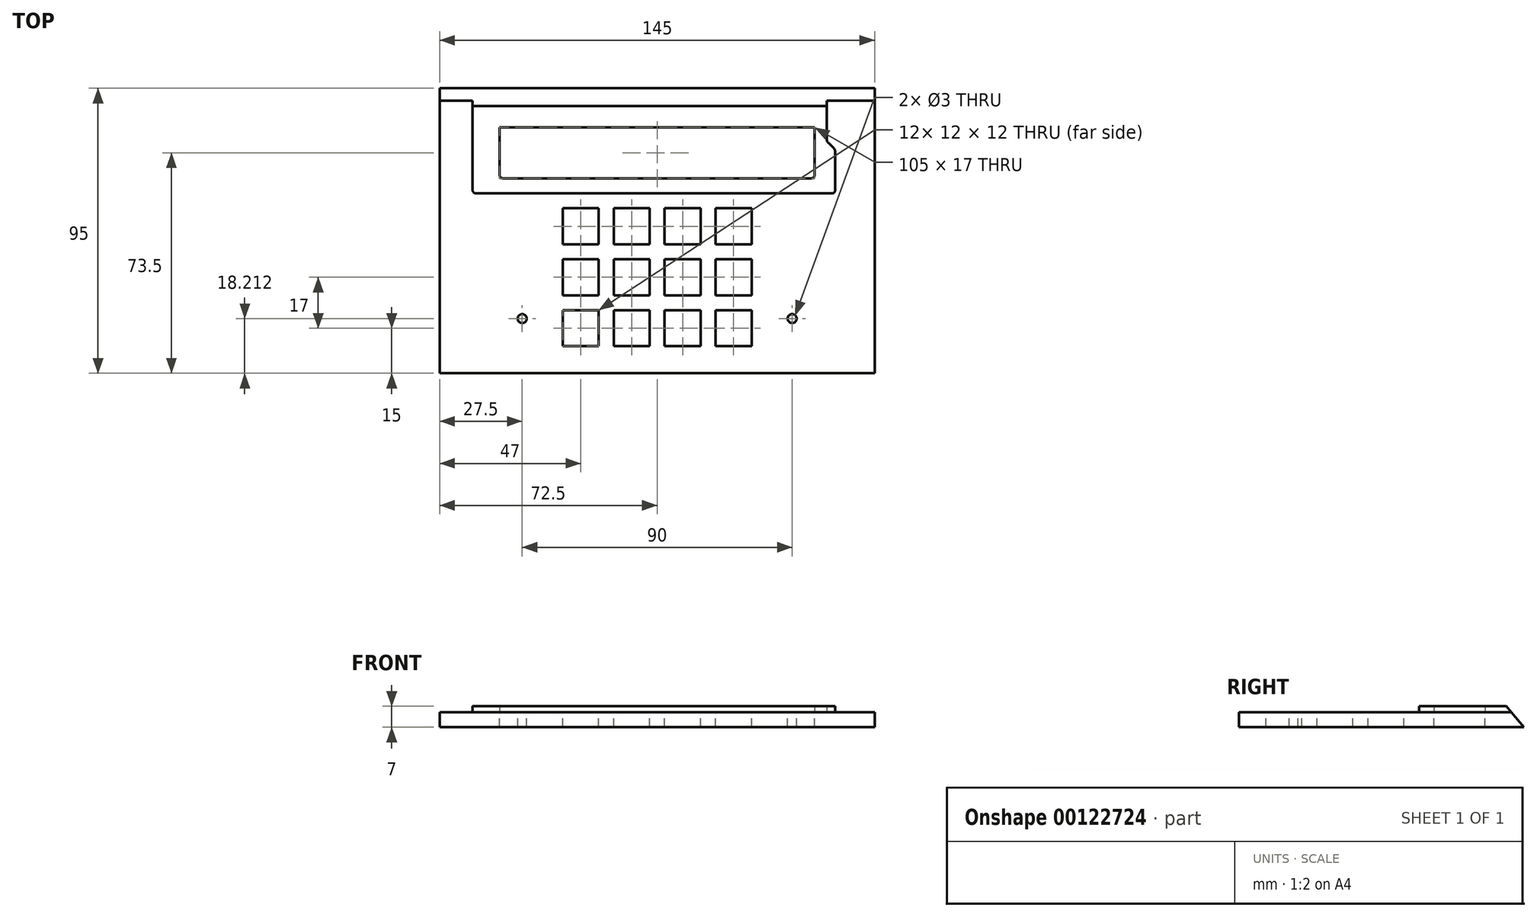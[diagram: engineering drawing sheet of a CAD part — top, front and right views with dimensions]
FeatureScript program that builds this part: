
annotation { "Feature Type Name" : "Feature", "Feature Type Description" : "" }
export const myFeature = defineFeature(function(context is Context, id is Id, definition is map)
    precondition{}
    {
        {
            var Q0;
            Q0=qCreatedBy(makeId("Top.planeOp"),FACE);
            var sketch = newSketch(context, id + "F0", { "sketchPlane" : qUnion([Q0])});
            skLineSegment(sketch, "E0.bottom", {"start": v(0, 0) * mm, "end": v(145, 0) * mm});
            skLineSegment(sketch, "E0.left", {"start": v(0, 0) * mm, "end": v(0, -95) * mm});
            skLineSegment(sketch, "E0.right", {"start": v(145, 0) * mm, "end": v(145, -95) * mm});
            skLineSegment(sketch, "E1.bottom", {"start": v(20, -13) * mm, "end": v(125, -13) * mm});
            skLineSegment(sketch, "E1.top", {"start": v(20, -30) * mm, "end": v(125, -30) * mm});
            skLineSegment(sketch, "E1.left", {"start": v(20, -13) * mm, "end": v(20, -30) * mm});
            skLineSegment(sketch, "E1.right", {"start": v(125, -13) * mm, "end": v(125, -30) * mm});
            skLineSegment(sketch, "E2.bottom", {"start": v(58, -40) * mm, "end": v(70, -40) * mm});
            skLineSegment(sketch, "E2.top", {"start": v(58, -52) * mm, "end": v(70, -52) * mm});
            skLineSegment(sketch, "E2.left", {"start": v(58, -40) * mm, "end": v(58, -52) * mm});
            skLineSegment(sketch, "E2.right", {"start": v(70, -40) * mm, "end": v(70, -52) * mm});
            skLineSegment(sketch, "E3.bottom", {"start": v(75, -40) * mm, "end": v(87, -40) * mm});
            skLineSegment(sketch, "E3.top", {"start": v(75, -52) * mm, "end": v(87, -52) * mm});
            skLineSegment(sketch, "E3.left", {"start": v(75, -40) * mm, "end": v(75, -52) * mm});
            skLineSegment(sketch, "E3.right", {"start": v(87, -40) * mm, "end": v(87, -52) * mm});
            skLineSegment(sketch, "E4.bottom", {"start": v(41, -40) * mm, "end": v(53, -40) * mm});
            skLineSegment(sketch, "E4.top", {"start": v(41, -52) * mm, "end": v(53, -52) * mm});
            skLineSegment(sketch, "E4.left", {"start": v(41, -40) * mm, "end": v(41, -52) * mm});
            skLineSegment(sketch, "E4.right", {"start": v(53, -40) * mm, "end": v(53, -52) * mm});
            skLineSegment(sketch, "E5.bottom", {"start": v(41, -57) * mm, "end": v(53, -57) * mm});
            skLineSegment(sketch, "E5.top", {"start": v(41, -69) * mm, "end": v(53, -69) * mm});
            skLineSegment(sketch, "E5.left", {"start": v(41, -57) * mm, "end": v(41, -69) * mm});
            skLineSegment(sketch, "E5.right", {"start": v(53, -57) * mm, "end": v(53, -69) * mm});
            skLineSegment(sketch, "E6.bottom", {"start": v(58, -57) * mm, "end": v(70, -57) * mm});
            skLineSegment(sketch, "E6.top", {"start": v(58, -69) * mm, "end": v(70, -69) * mm});
            skLineSegment(sketch, "E6.left", {"start": v(58, -57) * mm, "end": v(58, -69) * mm});
            skLineSegment(sketch, "E6.right", {"start": v(70, -57) * mm, "end": v(70, -69) * mm});
            skLineSegment(sketch, "E7", {"start": v(0, -95) * mm, "end": v(145, -95) * mm});
            skLineSegment(sketch, "E8", {"start": v(75, -57) * mm, "end": v(75, -69) * mm});
            skLineSegment(sketch, "E9", {"start": v(75, -69) * mm, "end": v(87, -69) * mm});
            skLineSegment(sketch, "E10", {"start": v(87, -69) * mm, "end": v(87, -57) * mm});
            skLineSegment(sketch, "E11", {"start": v(87, -57) * mm, "end": v(75, -57) * mm});
            skLineSegment(sketch, "E12.bottom", {"start": v(92, -57) * mm, "end": v(104, -57) * mm});
            skLineSegment(sketch, "E12.top", {"start": v(92, -69) * mm, "end": v(104, -69) * mm});
            skLineSegment(sketch, "E12.left", {"start": v(92, -57) * mm, "end": v(92, -69) * mm});
            skLineSegment(sketch, "E12.right", {"start": v(104, -57) * mm, "end": v(104, -69) * mm});
            skLineSegment(sketch, "E13.bottom", {"start": v(92, -40) * mm, "end": v(104, -40) * mm});
            skLineSegment(sketch, "E13.top", {"start": v(92, -52) * mm, "end": v(104, -52) * mm});
            skLineSegment(sketch, "E13.left", {"start": v(92, -40) * mm, "end": v(92, -52) * mm});
            skLineSegment(sketch, "E13.right", {"start": v(104, -40) * mm, "end": v(104, -52) * mm});
            skLineSegment(sketch, "E14.bottom", {"start": v(75, -74) * mm, "end": v(87, -74) * mm});
            skLineSegment(sketch, "E14.top", {"start": v(75, -86) * mm, "end": v(87, -86) * mm});
            skLineSegment(sketch, "E14.left", {"start": v(75, -74) * mm, "end": v(75, -86) * mm});
            skLineSegment(sketch, "E14.right", {"start": v(87, -74) * mm, "end": v(87, -86) * mm});
            skLineSegment(sketch, "E15.bottom", {"start": v(92, -74) * mm, "end": v(104, -74) * mm});
            skLineSegment(sketch, "E15.top", {"start": v(92, -86) * mm, "end": v(104, -86) * mm});
            skLineSegment(sketch, "E15.left", {"start": v(92, -74) * mm, "end": v(92, -86) * mm});
            skLineSegment(sketch, "E15.right", {"start": v(104, -74) * mm, "end": v(104, -86) * mm});
            skLineSegment(sketch, "E16.bottom", {"start": v(58, -74) * mm, "end": v(70, -74) * mm});
            skLineSegment(sketch, "E16.top", {"start": v(58, -86) * mm, "end": v(70, -86) * mm});
            skLineSegment(sketch, "E16.left", {"start": v(58, -74) * mm, "end": v(58, -86) * mm});
            skLineSegment(sketch, "E16.right", {"start": v(70, -74) * mm, "end": v(70, -86) * mm});
            skLineSegment(sketch, "E17.bottom", {"start": v(41, -74) * mm, "end": v(53, -74) * mm});
            skLineSegment(sketch, "E17.top", {"start": v(41, -86) * mm, "end": v(53, -86) * mm});
            skLineSegment(sketch, "E17.left", {"start": v(41, -74) * mm, "end": v(41, -86) * mm});
            skLineSegment(sketch, "E17.right", {"start": v(53, -74) * mm, "end": v(53, -86) * mm});
            skCircle(sketch, "E18", {"center": v(27.5, -76.79) * mm, "radius": 8.5 * mm, "construction": true});
            skCircle(sketch, "E19", {"center": v(27.5, -76.79) * mm, "radius": 1.5 * mm});
            skCircle(sketch, "E20", {"center": v(117.5, -76.79) * mm, "radius": 8.5 * mm, "construction": true});
            skCircle(sketch, "E21", {"center": v(117.5, -76.79) * mm, "radius": 1.5 * mm});
            skSolve(sketch);
        }
        {
            var Q0;
            Q0=makeQuery(id+"F0.imprint","IMPRINT",FACE,{"disambiguationData":[TD([[makeQuery(id+"F0.imprint","IMPRINT",EDGE,{"derivedFrom":sQuery(id+"F0.wireOp",EDGE,"E0.bottom")}),-1.0]])]});
            extrude(context, id + "F1", {"entities" : qUnion([Q0]), "oppositeDirection" : true, "depth" : 5 * mm});
        }
        {
            var Q0;
            Q0=qCreatedBy(makeId("Top.planeOp"),FACE);
            var sketch = newSketch(context, id + "F2", { "sketchPlane" : qUnion([Q0])});
            skLineSegment(sketch, "E22.bottom", {"start": v(11, 0) * mm, "end": v(129, 0) * mm});
            skLineSegment(sketch, "E22.top", {"start": v(12, -35) * mm, "end": v(130.86, -35) * mm});
            skLineSegment(sketch, "E22.left", {"start": v(11, 0) * mm, "end": v(11, -34) * mm});
            skLineSegment(sketch, "E22.right", {"start": v(131.86, -21.26) * mm, "end": v(131.86, -34) * mm});
            skLineSegment(sketch, "E23.bottom", {"start": v(20, -13) * mm, "end": v(125, -13) * mm});
            skLineSegment(sketch, "E23.top", {"start": v(21, -30) * mm, "end": v(124, -30) * mm});
            skLineSegment(sketch, "E23.left", {"start": v(20, -13) * mm, "end": v(20, -29) * mm});
            skLineSegment(sketch, "E23.right", {"start": v(125, -13) * mm, "end": v(125, -29) * mm});
            skLineSegment(sketch, "E24", {"start": v(129, 0) * mm, "end": v(129, -16.83) * mm});
            skLineSegment(sketch, "E25", {"start": v(129.63, -18.29) * mm, "end": v(131.24, -19.8) * mm});
            skPoint(sketch, "E26.visualSharp", {"position": v(129, -17.7) * mm});
            skArc(sketch, "E26.filletArc", {"start": v(129, -16.83) * mm, "mid": v(129.16, -17.62) * mm, "end": v(129.63, -18.29) * mm});
            skPoint(sketch, "E27.visualSharp", {"position": v(131.86, -20.4) * mm});
            skArc(sketch, "E27.filletArc", {"start": v(131.86, -21.26) * mm, "mid": v(131.7, -20.46) * mm, "end": v(131.24, -19.8) * mm});
            skPoint(sketch, "E28.visualSharp", {"position": v(20, -30) * mm});
            skArc(sketch, "E28.filletArc", {"start": v(20, -29) * mm, "mid": v(20.3, -29.7) * mm, "end": v(21, -30) * mm});
            skPoint(sketch, "E29.visualSharp", {"position": v(125, -30) * mm});
            skArc(sketch, "E29.filletArc", {"start": v(124, -30) * mm, "mid": v(124.7, -29.7) * mm, "end": v(125, -29) * mm});
            skPoint(sketch, "E30.visualSharp", {"position": v(11, -35) * mm});
            skArc(sketch, "E30.filletArc", {"start": v(11, -34) * mm, "mid": v(11.3, -34.7) * mm, "end": v(12, -35) * mm});
            skPoint(sketch, "E31.visualSharp", {"position": v(131.86, -35) * mm});
            skArc(sketch, "E31.filletArc", {"start": v(130.86, -35) * mm, "mid": v(131.57, -34.7) * mm, "end": v(131.86, -34) * mm});
            skSolve(sketch);
        }
        {
            var Q0;
            Q0=qSketchRegion(id+"F2",true);
            extrude(context, id + "F3", {"entities" : qUnion([Q0]), "operationType" : NewBodyOperationType.ADD, "depth" : 2 * mm});
        }
        {
            var Q0;
            Q0=makeQuery(id+"F1.opExtrude","SWEPT_FACE",FACE,{"disambiguationData":[OSD([sQuery(id+"F0.wireOp",EDGE,"E0.left")])]});
            var sketch = newSketch(context, id + "F4", { "sketchPlane" : qUnion([Q0])});
            skLineSegment(sketch, "E32", {"start": v(0, -5) * mm, "end": v(8.4, 5) * mm});
            skLineSegment(sketch, "E33", {"start": v(8.4, 5) * mm, "end": v(0, 5) * mm});
            skLineSegment(sketch, "E34", {"start": v(0, 5) * mm, "end": v(0, -5) * mm});
            skSolve(sketch);
        }
        {
            var Q0;
            Q0=qSketchRegion(id+"F4",true);
            extrude(context, id + "F5", {"entities" : qUnion([Q0]), "operationType" : NewBodyOperationType.REMOVE, "oppositeDirection" : true, "depth" : 200 * mm});
        }
    });
